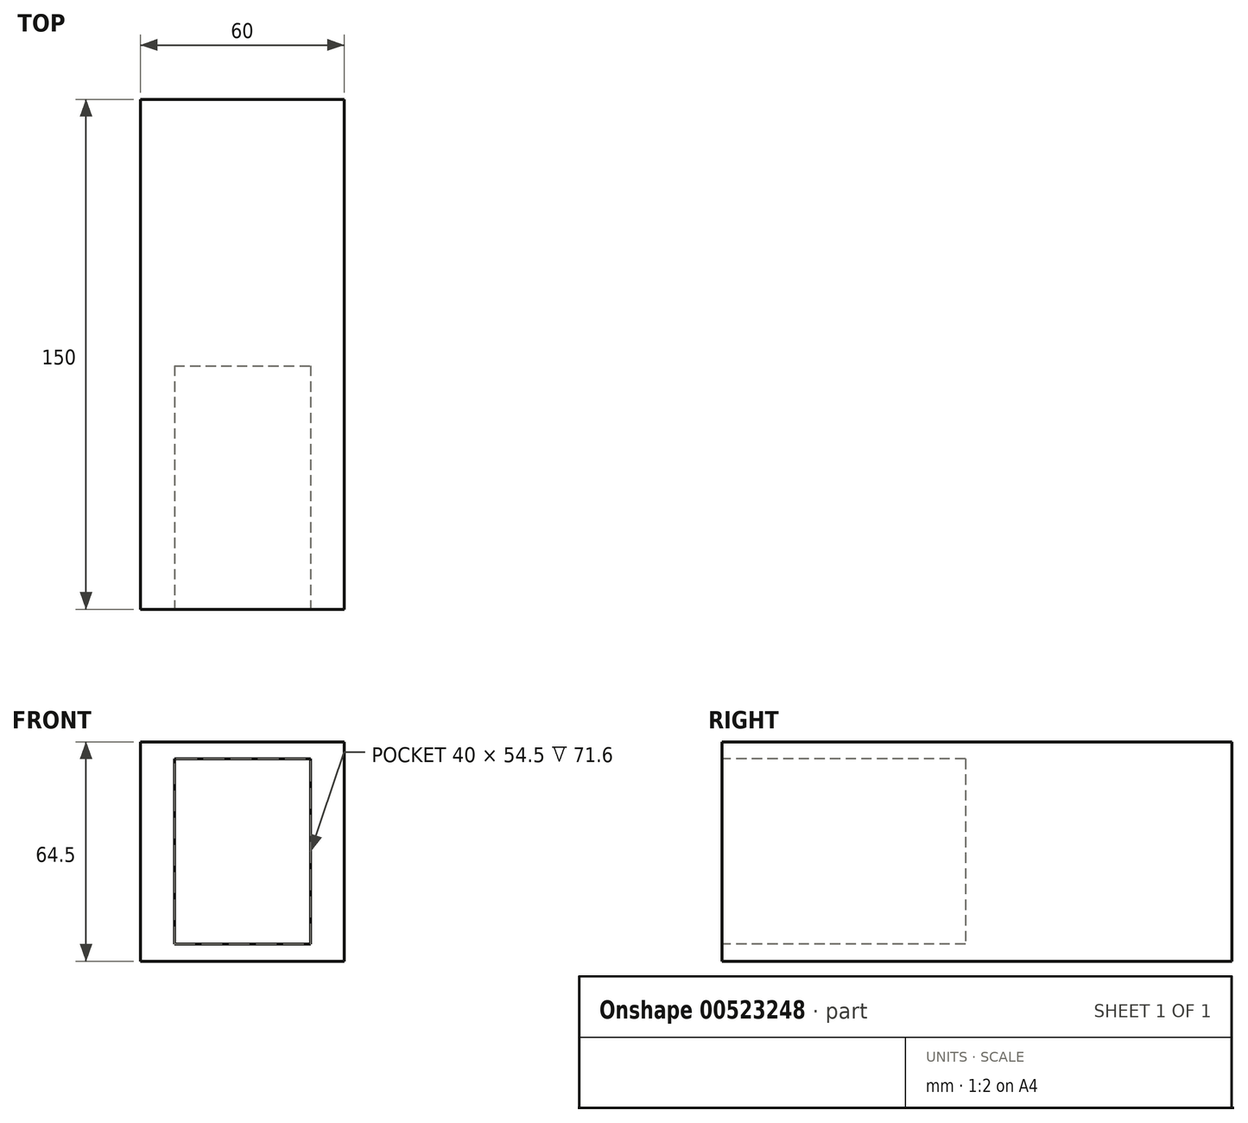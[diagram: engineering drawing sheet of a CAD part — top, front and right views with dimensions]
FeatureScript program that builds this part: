
annotation { "Feature Type Name" : "Feature", "Feature Type Description" : "" }
export const myFeature = defineFeature(function(context is Context, id is Id, definition is map)
    precondition{}
    {
        {
            var Q0;
            Q0=qCreatedBy(makeId("Top.planeOp"),FACE);
            var sketch = newSketch(context, id + "F0", { "sketchPlane" : qUnion([Q0])});
            skLineSegment(sketch, "E0.bottom", {"start": v(-36.38, -35.04) * mm, "end": v(23.62, -35.04) * mm});
            skLineSegment(sketch, "E0.top", {"start": v(-36.38, 114.96) * mm, "end": v(23.62, 114.96) * mm});
            skLineSegment(sketch, "E0.left", {"start": v(-36.38, -35.04) * mm, "end": v(-36.38, 114.96) * mm});
            skLineSegment(sketch, "E0.right", {"start": v(23.62, -35.04) * mm, "end": v(23.62, 114.96) * mm});
            skSolve(sketch);
        }
        {
            var Q0;
            Q0 = qSketchRegion(id + "F0", true);
            extrude(context, id + "F1", {"entities" : qUnion([Q0]), "depth" : 64.5 * mm, "offsetDistance" : 25 * mm});
        }
        {
            var Q0;
            Q0=makeQuery(id+"F1.opExtrude","SWEPT_FACE",FACE,{"disambiguationData":[OSD([sQuery(id+"F0.wireOp",EDGE,"E0.bottom")])]});
            var sketch = newSketch(context, id + "F2", { "sketchPlane" : qUnion([Q0])});
            skLineSegment(sketch, "E1.bottom", {"start": v(-26.38, 59.5) * mm, "end": v(13.62, 59.5) * mm});
            skLineSegment(sketch, "E1.top", {"start": v(-26.38, 5) * mm, "end": v(13.62, 5) * mm});
            skLineSegment(sketch, "E1.left", {"start": v(-26.38, 59.5) * mm, "end": v(-26.38, 5) * mm});
            skLineSegment(sketch, "E1.right", {"start": v(13.62, 59.5) * mm, "end": v(13.62, 5) * mm});
            skSolve(sketch);
        }
        {
            var Q0;
            Q0 = qSketchRegion(id + "F2", true);
            extrude(context, id + "F3", {"entities" : qUnion([Q0]), "operationType" : NewBodyOperationType.REMOVE, "oppositeDirection" : true, "depth" : 71.6 * mm, "offsetDistance" : 25 * mm});
        }
    });
